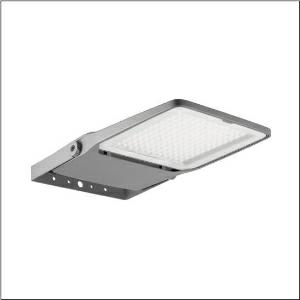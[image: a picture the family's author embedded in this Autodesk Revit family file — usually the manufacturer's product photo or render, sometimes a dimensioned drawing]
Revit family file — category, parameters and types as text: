
# Revit family: floodlight_fl_20_midi___rs05_5xa7682g2h2ac_5173
name_source: partatom
category: Lighting Fixtures
units: mm (PartAtom-declared; Revit-internal decimal feet)

## family parameters
Cut with Voids When Loaded = No
Host = Face
Light Source = No
Part Type = Normal
Room Calculation Point = No
Round Connector Dimension = Use Diameter
Shared = No

## types (1)
- --- (1 x LED 4000K / CRI = 70 (unbekannt), 38380 lm, 4000K)
    Apparent Load = 306 VA
    CIE Flux Codes = 81 94 99 100 100
    Color Rendering = 70
    Color Temperature = 4000K
    Default Elevation = 1800 mm
    Description = Floodlight FL 20 midi, floodlight, primary light control with lens, of plastic, primary optical cover: protective disc, of toughened safety glass, transparent, light distribution: RS05, light emission: direct distribution, primary light characteristic: rotationally symmetric, installation type: surface-mounted, LED High Power LED, rated luminous flux: 38.380 lm, light colour: 740, colour temperature: 4000K, control gear: ECG Plus, control: overheat protection, power reduction, digital communication interface, time-dependent luminous flux control, flexible luminous flux parameterisation, electronic power reduction, with terminal, 10-pole, max. 2.5mm², mains connection: 220..240V, AC, 50/60Hz, rated input power: 306W, LED unit, of diecast aluminium, powder-coated, Siteco® metallic grey (DB 702S), length: 731 mm, width: 450 mm, height: 76mm, housing frame, of diecast aluminium, powder-coated, Siteco® metallic grey (DB 702S), wall fastening, DALIprotection rating (complete): IP66, insulation class (complete): insulation class II (safety insulation), certification: CE, ENEC, VDE, protection symbol: D, permissible ambient temperature for indoor applications: -40..+40°C, permissible ambient temperature for outdoor applications: -40..+50°C, standard: DIN EN 12944, packaging unit: 1 piece

Light Distribution: RS05
    Height = 76 mm
    Lamp = 1 x LED 4000K / CRI >= 70 (unbekannt)
    Lamp Light Flux = 38380 lm
    Lamp count = 1
    Length = 731 mm
    Luminous efficacy = 126 lm/W
    Manufacturer = Siteco
    ModVariant = No
    Model = 5XA7682G2H2AC
    Number of Poles = 1
    OnlyDefault = Yes
    Power Factor = 1
    Product Name = Floodlight FL 20 midi | RS05
    Product group = floodlight | pylon top
    ProductGroupID = 6101
    Protection Class = Protection class II
    Protection Degree = IP 66
    RLX_Detail_Level = 1
    RlxData = <blob elided: 86629 chars, md5=bf86c7fd>
    Socket = socket
    Standby Power = 0 W
    System Light Flux = 38380 lm
    System Power = 306 W
    Type Comments = factory setting: luminous flux: 100 % | dim-lin: 254 | 700 mA
    Type Image = l_1005944.jpg
    URL = http://relux.com
    VarID = @adj_141669
    Voltage = 0 V
    Weight = 0.00 kg
    Width = 450 mm

## geometry (parser evidence)
native form markers: Blend x4, Sweep x10
no freeform markers — native parametric forms only
